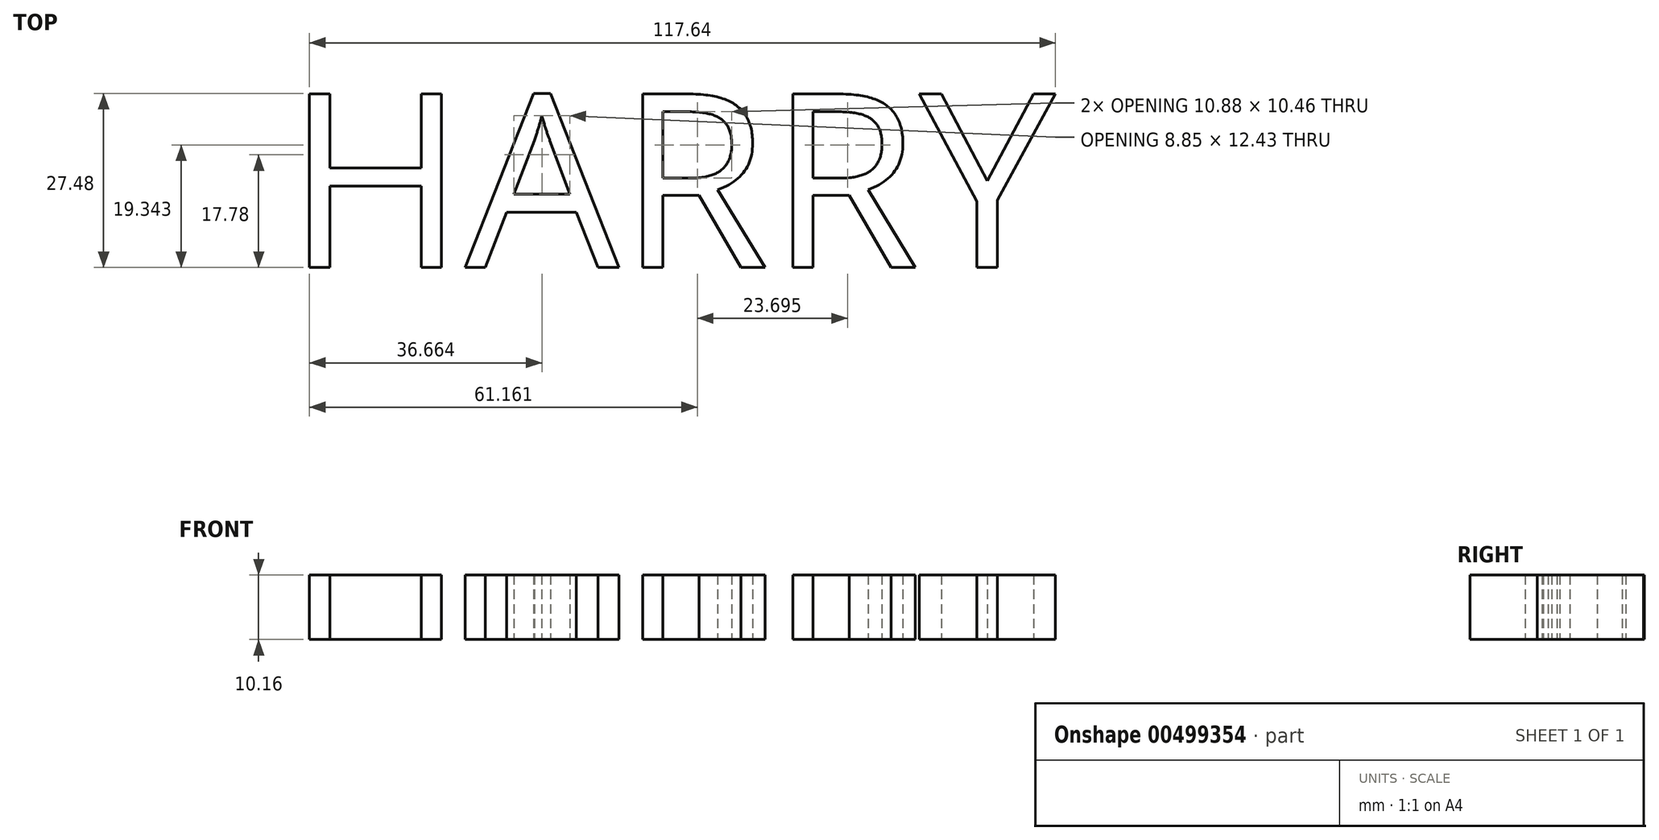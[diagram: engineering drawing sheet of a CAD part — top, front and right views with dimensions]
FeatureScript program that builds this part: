
annotation { "Feature Type Name" : "Feature", "Feature Type Description" : "" }
export const myFeature = defineFeature(function(context is Context, id is Id, definition is map)
    precondition{}
    {
        {
            var Q0;
            Q0=qCreatedBy(makeId("Top.planeOp"),FACE);
            var sketch = newSketch(context, id + "F0", { "sketchPlane" : qUnion([Q0])});
            skText(sketch, "E0", { "text": "HARRY", "fontName": "OpenSans-Regular.ttf"});
            const initialGuessF0  = {"E0": [-0.0613, -0.01483, 1, 0, 0.0276]};
            skSetInitialGuess(sketch, initialGuessF0);
            skSolve(sketch);
        }
        {
            var Q0;
            Q0 = qSketchRegion(id + "F0", true);
            extrude(context, id + "F1", {"entities" : qUnion([Q0]), "depth" : 10.16 * mm});
        }
    });
